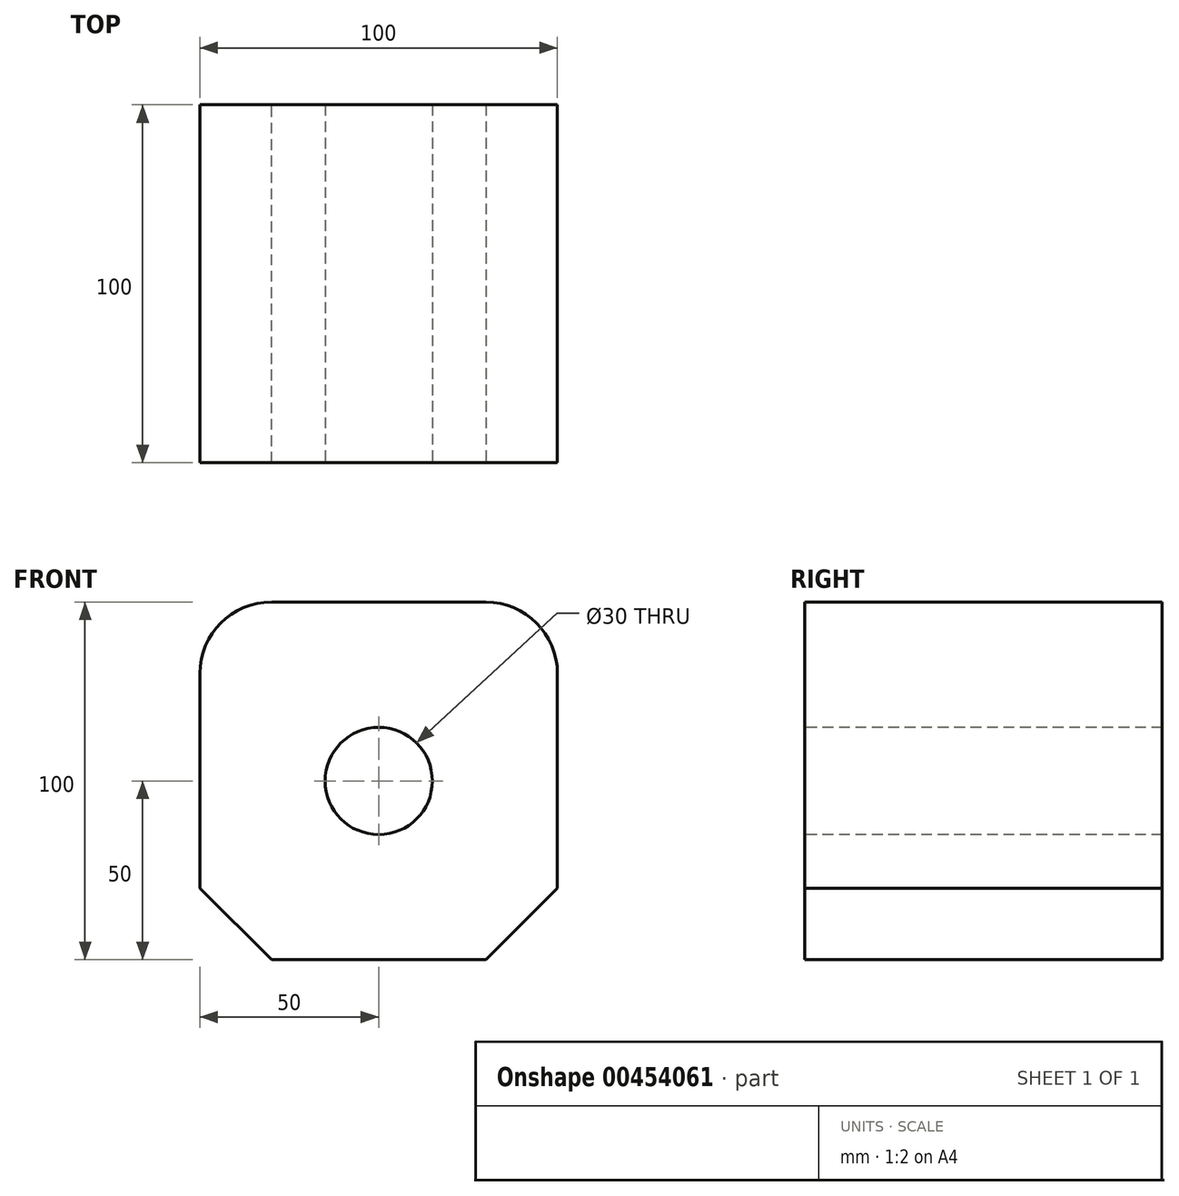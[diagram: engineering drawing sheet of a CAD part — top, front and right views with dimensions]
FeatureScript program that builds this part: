
annotation { "Feature Type Name" : "Feature", "Feature Type Description" : "" }
export const myFeature = defineFeature(function(context is Context, id is Id, definition is map)
    precondition{}
    {
        {
            var Q0;
            Q0=qCreatedBy(makeId("Front.planeOp"),FACE);
            var sketch = newSketch(context, id + "F0", { "sketchPlane" : qUnion([Q0])});
            skLineSegment(sketch, "E0.bottom", {"start": v(50, -50) * mm, "end": v(-50, -50) * mm});
            skLineSegment(sketch, "E0.top", {"start": v(50, 50) * mm, "end": v(-50, 50) * mm});
            skLineSegment(sketch, "E0.left", {"start": v(50, -50) * mm, "end": v(50, 50) * mm});
            skLineSegment(sketch, "E0.right", {"start": v(-50, -50) * mm, "end": v(-50, 50) * mm});
            skPoint(sketch, "E0.middle", {"position": v(0, 0) * mm});
            skSolve(sketch);
        }
        {
            var Q0;
            Q0 = qSketchRegion(id + "F0", true);
            extrude(context, id + "F1", {"entities" : qUnion([Q0]), "depth" : 100 * mm});
        }
        {
            var Q0;
            Q0=makeQuery(id+"F1.opExtrude","CAP_FACE",FACE,{"disambiguationData":[OSD([sQuery(id+"F0.wireOp",EDGE,"E0.bottom"),sQuery(id+"F0.wireOp",EDGE,"E0.top"),sQuery(id+"F0.wireOp",EDGE,"E0.left"),sQuery(id+"F0.wireOp",EDGE,"E0.right")])],"isStart":false});
            var sketch = newSketch(context, id + "F2", { "sketchPlane" : qUnion([Q0])});
            skCircle(sketch, "E1", {"center": v(0, 0) * mm, "radius": 15 * mm});
            skSolve(sketch);
        }
        {
            var Q0;
            Q0=makeQuery(id+"F2.imprint","IMPRINT",FACE,{"disambiguationData":[TD([[makeQuery(id+"F2.imprint","IMPRINT",EDGE,{"derivedFrom":sQuery(id+"F2.wireOp",EDGE,"E1")}),1.0]])]});
            extrude(context, id + "F3", {"entities" : qUnion([Q0]), "operationType" : NewBodyOperationType.REMOVE, "endBound" : BoundingType.THROUGH_ALL, "oppositeDirection" : true, "depth" : 100 * mm});
        }
        {
            var Q0;
            Q0=makeQuery(id+"F1.opExtrude","SWEPT_EDGE",EDGE,{"disambiguationData":[OSD([sQuery(id+"F0.wireOp",EDGE,"E0.top"),sQuery(id+"F0.wireOp",EDGE,"E0.right")])]});
            var Q1;
            Q1=makeQuery(id+"F1.opExtrude","SWEPT_EDGE",EDGE,{"disambiguationData":[OSD([sQuery(id+"F0.wireOp",EDGE,"E0.top"),sQuery(id+"F0.wireOp",EDGE,"E0.left")])]});
            fillet(context, id + "F4", {"entities" : qUnion([Q0, Q1]), "radius" : 20 * mm, "tangentPropagation" : true, "allowEdgeOverflow" : false});
        }
        {
            var Q0;
            Q0=makeQuery(id+"F1.opExtrude","SWEPT_EDGE",EDGE,{"disambiguationData":[OSD([sQuery(id+"F0.wireOp",EDGE,"E0.bottom"),sQuery(id+"F0.wireOp",EDGE,"E0.right")])]});
            var Q1;
            Q1=makeQuery(id+"F1.opExtrude","SWEPT_EDGE",EDGE,{"disambiguationData":[OSD([sQuery(id+"F0.wireOp",EDGE,"E0.bottom"),sQuery(id+"F0.wireOp",EDGE,"E0.left")])]});
            chamfer(context, id + "F5", {"entities" : qUnion([Q0, Q1]), "width" : 20 * mm, "tangentPropagation" : true});
        }
    });
